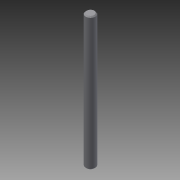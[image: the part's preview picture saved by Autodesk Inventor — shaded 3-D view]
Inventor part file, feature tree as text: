
AUTODESK INVENTOR PART (.ipt)
format: ipt  version: 2015 (Build 190159000, 159)  size: 82,432 bytes
history: native  units: in
note: dims shown in document units (in); Inventor stores cm internally (conversion verified against a paired STEP export)
features: other x3, extrude x1, chamfer x1, sketch x1
ambient origin geometry x8: Origin, YZ Plane, XZ Plane, XY Plane, X Axis, Y Axis, Z Axis, Center Point
bodies: Solid1 (feature_tree)
feature tree (6):
  other  "Axle-100mm - 739088.ipt"
  extrude  "Extrusion1"  Depth=0.3937in TaperAngle=0.0deg
  chamfer  "Chamfer1"  Distance=0.0197in Angle=45.0deg
  other  "tetrix_739088_2013::Axle-100mm - 739088.ipt"
  other  "TaggingFeature1"
  sketch  "Sketch1"  dims[d0=0.3937in d1=1.378in d2=0.0in d3=0.0197in d4=0.125in d5=45.0deg]
